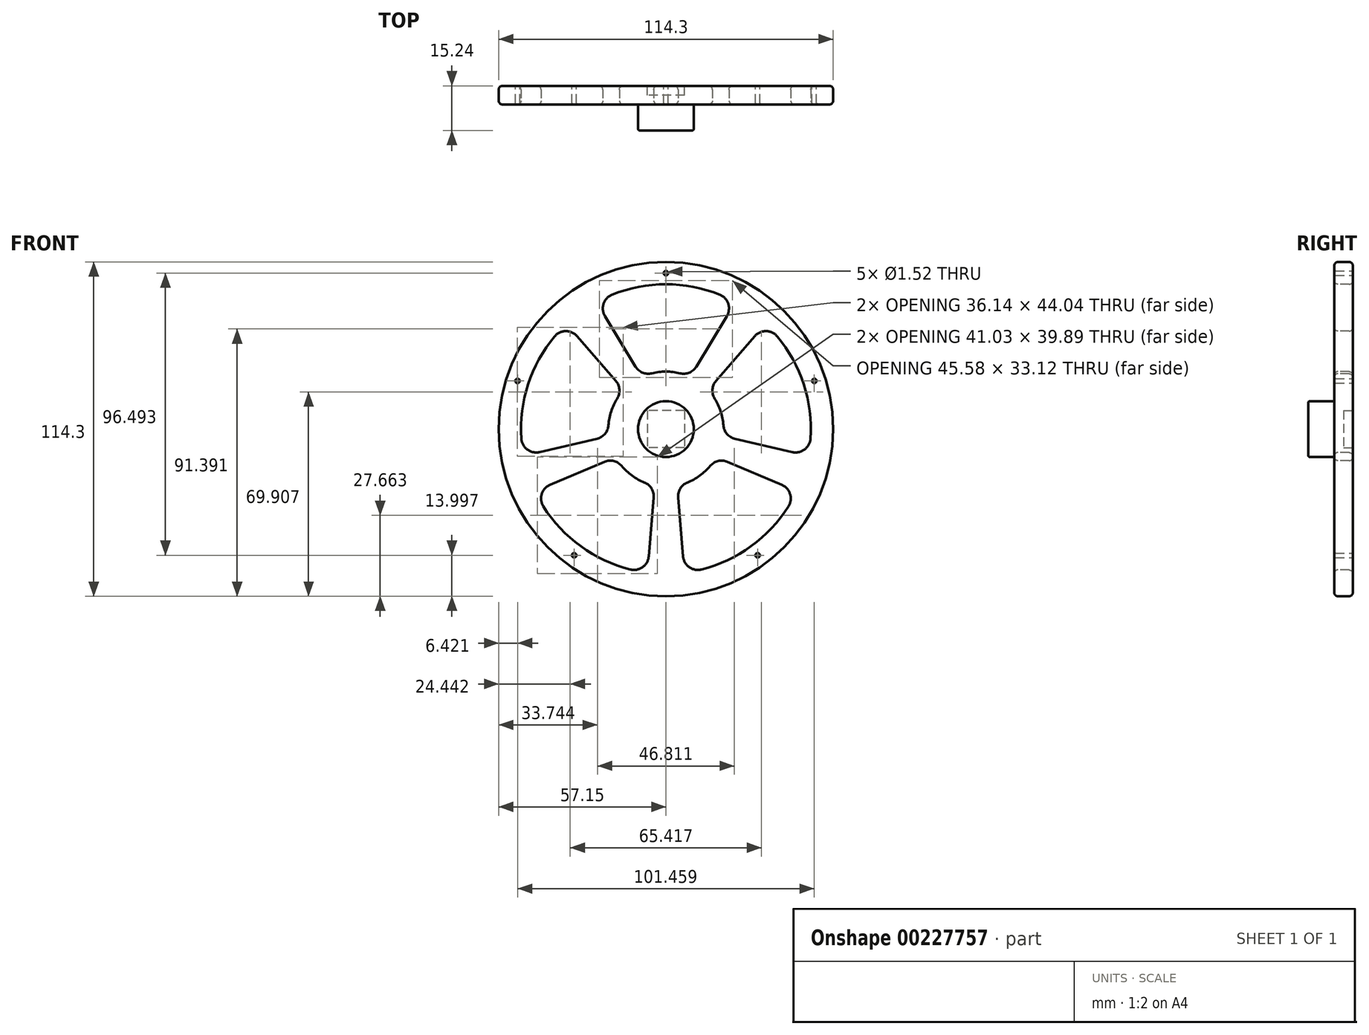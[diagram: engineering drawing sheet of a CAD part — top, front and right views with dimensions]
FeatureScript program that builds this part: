
annotation { "Feature Type Name" : "Feature", "Feature Type Description" : "" }
export const myFeature = defineFeature(function(context is Context, id is Id, definition is map)
    precondition{}
    {
        {
            var Q0;
            Q0=qCreatedBy(makeId("Front.planeOp"),FACE);
            var sketch = newSketch(context, id + "F0", { "sketchPlane" : qUnion([Q0])});
            skCircle(sketch, "E0", {"center": v(0, 0) * mm, "radius": 57.15 * mm});
            skSolve(sketch);
        }
        {
            var Q0;
            Q0=qSketchRegion(id+"F0",true);
            extrude(context, id + "F1", {"entities" : qUnion([Q0]), "depth" : 6.35 * mm});
        }
        {
            var Q0;
            Q0=makeQuery(id+"F1.opExtrude","CAP_FACE",FACE,{"disambiguationData":[OSD([sQuery(id+"F0.wireOp",EDGE,"E0")])],"isStart":false});
            var sketch = newSketch(context, id + "F2", { "sketchPlane" : qUnion([Q0])});
            skCircle(sketch, "E1", {"center": v(0, 0) * mm, "radius": 9.53 * mm});
            skSolve(sketch);
        }
        {
            var Q0;
            Q0=qSketchRegion(id+"F2",true);
            extrude(context, id + "F3", {"entities" : qUnion([Q0]), "operationType" : NewBodyOperationType.ADD, "depth" : 8.9 * mm});
        }
        {
            var Q0;
            Q0=makeQuery(id+"F1.opExtrude","CAP_FACE",FACE,{"disambiguationData":[OSD([sQuery(id+"F0.wireOp",EDGE,"E0")])],"isStart":true});
            var sketch = newSketch(context, id + "F4", { "sketchPlane" : qUnion([Q0])});
            skCircle(sketch, "E2", {"center": v(0, 53.34) * mm, "radius": 0.76 * mm});
            skCircle(sketch, "E3.1.0", {"center": v(-50.73, 16.48) * mm, "radius": 0.76 * mm});
            skCircle(sketch, "E3.2.0", {"center": v(-31.35, -43.15) * mm, "radius": 0.76 * mm});
            skCircle(sketch, "E3.3.0", {"center": v(31.35, -43.15) * mm, "radius": 0.76 * mm});
            skCircle(sketch, "E3.4.0", {"center": v(50.73, 16.48) * mm, "radius": 0.76 * mm});
            skPoint(sketch, "E3.center", {"position": v(0, 0) * mm});
            skSolve(sketch);
        }
        {
            var Q0;
            Q0=qSketchRegion(id+"F4",true);
            extrude(context, id + "F5", {"entities" : qUnion([Q0]), "operationType" : NewBodyOperationType.REMOVE, "endBound" : BoundingType.THROUGH_ALL, "oppositeDirection" : true, "depth" : 25.4 * mm});
        }
        {
            var Q0;
            Q0=makeQuery(id+"F1.opExtrude","CAP_FACE",FACE,{"disambiguationData":[OSD([sQuery(id+"F0.wireOp",EDGE,"E0")])],"isStart":false});
            var sketch = newSketch(context, id + "F6", { "sketchPlane" : qUnion([Q0])});
            skArc(sketch, "E4", {"start": v(-14.43, 13.38) * mm, "mid": v(-18.72, 6.08) * mm, "end": v(-19.54, -2.34) * mm});
            skArc(sketch, "E5", {"start": v(-34.01, 36) * mm, "mid": v(-47.1, 15.3) * mm, "end": v(-48.68, -9.14) * mm});
            skLineSegment(sketch, "E6", {"start": v(-3.8, -19.31) * mm, "end": v(-6.35, -49.12) * mm});
            skLineSegment(sketch, "E7", {"start": v(3.8, -19.31) * mm, "end": v(6.35, -49.12) * mm});
            skLineSegment(sketch, "E8.1.0", {"start": v(17.2, -9.6) * mm, "end": v(44.75, -21.22) * mm});
            skLineSegment(sketch, "E8.1.1", {"start": v(19.54, -2.34) * mm, "end": v(48.68, -9.14) * mm});
            skLineSegment(sketch, "E8.2.0", {"start": v(14.43, 13.38) * mm, "end": v(34.01, 36) * mm});
            skLineSegment(sketch, "E8.2.1", {"start": v(8.27, 17.86) * mm, "end": v(23.74, 43.47) * mm});
            skLineSegment(sketch, "E8.3.0", {"start": v(-8.27, 17.86) * mm, "end": v(-23.74, 43.47) * mm});
            skLineSegment(sketch, "E8.3.1", {"start": v(-14.43, 13.38) * mm, "end": v(-34.01, 36) * mm});
            skLineSegment(sketch, "E8.4.0", {"start": v(-19.54, -2.34) * mm, "end": v(-48.68, -9.14) * mm});
            skLineSegment(sketch, "E8.4.1", {"start": v(-17.2, -9.6) * mm, "end": v(-44.75, -21.22) * mm});
            skArc(sketch, "E9.trimOffspring", {"start": v(8.27, 17.86) * mm, "mid": v(0, 19.69) * mm, "end": v(-8.27, 17.86) * mm});
            skArc(sketch, "E10.trimOffspring", {"start": v(23.74, 43.47) * mm, "mid": v(0, 49.53) * mm, "end": v(-23.74, 43.47) * mm});
            skArc(sketch, "E11.trimOffspring", {"start": v(48.68, -9.14) * mm, "mid": v(47.1, 15.3) * mm, "end": v(34.01, 36) * mm});
            skArc(sketch, "E12.trimOffspring", {"start": v(19.54, -2.34) * mm, "mid": v(18.72, 6.08) * mm, "end": v(14.43, 13.38) * mm});
            skArc(sketch, "E13.trimOffspring", {"start": v(3.81, -19.31) * mm, "mid": v(11.57, -15.93) * mm, "end": v(17.2, -9.6) * mm});
            skArc(sketch, "E14.trimOffspring", {"start": v(6.35, -49.12) * mm, "mid": v(29.11, -40.07) * mm, "end": v(44.75, -21.22) * mm});
            skArc(sketch, "E15.trimOffspring", {"start": v(-44.75, -21.22) * mm, "mid": v(-29.11, -40.07) * mm, "end": v(-6.35, -49.12) * mm});
            skArc(sketch, "E16.trimOffspring", {"start": v(-17.2, -9.6) * mm, "mid": v(-11.57, -15.93) * mm, "end": v(-3.81, -19.31) * mm});
            skSolve(sketch);
        }
        {
            var Q0;
            Q0=qSketchRegion(id+"F6",true);
            extrude(context, id + "F7", {"entities" : qUnion([Q0]), "operationType" : NewBodyOperationType.REMOVE, "oppositeDirection" : true, "depth" : 25.4 * mm});
        }
        {
            var Q0;
            Q0=makeQuery(id+"F7.boolean.opBoolean","COPY",EDGE,{"derivedFrom":makeQuery(id+"F7.opExtrude","SWEPT_EDGE",EDGE,{"disambiguationData":[OSD([sQuery(id+"F6.wireOp",EDGE,"E8.3.0"),sQuery(id+"F6.wireOp",EDGE,"E9.trimOffspring")])]})});
            var Q1;
            Q1=makeQuery(id+"F7.boolean.opBoolean","COPY",EDGE,{"derivedFrom":makeQuery(id+"F7.opExtrude","SWEPT_EDGE",EDGE,{"disambiguationData":[OSD([sQuery(id+"F6.wireOp",EDGE,"E8.2.1"),sQuery(id+"F6.wireOp",EDGE,"E9.trimOffspring")])]})});
            var Q2;
            Q2=makeQuery(id+"F7.boolean.opBoolean","COPY",EDGE,{"derivedFrom":makeQuery(id+"F7.opExtrude","SWEPT_EDGE",EDGE,{"disambiguationData":[OSD([sQuery(id+"F6.wireOp",EDGE,"E8.3.0"),sQuery(id+"F6.wireOp",EDGE,"E10.trimOffspring")])]})});
            var Q3;
            Q3=makeQuery(id+"F7.boolean.opBoolean","COPY",EDGE,{"derivedFrom":makeQuery(id+"F7.opExtrude","SWEPT_EDGE",EDGE,{"disambiguationData":[OSD([sQuery(id+"F6.wireOp",EDGE,"E8.2.1"),sQuery(id+"F6.wireOp",EDGE,"E10.trimOffspring")])]})});
            var Q4;
            Q4=makeQuery(id+"F7.boolean.opBoolean","COPY",EDGE,{"derivedFrom":makeQuery(id+"F7.opExtrude","SWEPT_EDGE",EDGE,{"disambiguationData":[OSD([sQuery(id+"F6.wireOp",EDGE,"E8.2.0"),sQuery(id+"F6.wireOp",EDGE,"E11.trimOffspring")])]})});
            var Q5;
            Q5=makeQuery(id+"F7.boolean.opBoolean","COPY",EDGE,{"derivedFrom":makeQuery(id+"F7.opExtrude","SWEPT_EDGE",EDGE,{"disambiguationData":[OSD([sQuery(id+"F6.wireOp",EDGE,"E8.2.0"),sQuery(id+"F6.wireOp",EDGE,"E12.trimOffspring")])]})});
            var Q6;
            Q6=makeQuery(id+"F7.boolean.opBoolean","COPY",EDGE,{"derivedFrom":makeQuery(id+"F7.opExtrude","SWEPT_EDGE",EDGE,{"disambiguationData":[OSD([sQuery(id+"F6.wireOp",EDGE,"E8.1.1"),sQuery(id+"F6.wireOp",EDGE,"E12.trimOffspring")])]})});
            var Q7;
            Q7=makeQuery(id+"F7.boolean.opBoolean","COPY",EDGE,{"derivedFrom":makeQuery(id+"F7.opExtrude","SWEPT_EDGE",EDGE,{"disambiguationData":[OSD([sQuery(id+"F6.wireOp",EDGE,"E8.1.1"),sQuery(id+"F6.wireOp",EDGE,"E11.trimOffspring")])]})});
            var Q8;
            Q8=makeQuery(id+"F7.boolean.opBoolean","COPY",EDGE,{"derivedFrom":makeQuery(id+"F7.opExtrude","SWEPT_EDGE",EDGE,{"disambiguationData":[OSD([sQuery(id+"F6.wireOp",EDGE,"E8.1.0"),sQuery(id+"F6.wireOp",EDGE,"E14.trimOffspring")])]})});
            var Q9;
            Q9=makeQuery(id+"F7.boolean.opBoolean","COPY",EDGE,{"derivedFrom":makeQuery(id+"F7.opExtrude","SWEPT_EDGE",EDGE,{"disambiguationData":[OSD([sQuery(id+"F6.wireOp",EDGE,"E7"),sQuery(id+"F6.wireOp",EDGE,"E14.trimOffspring")])]})});
            var Q10;
            Q10=makeQuery(id+"F7.boolean.opBoolean","COPY",EDGE,{"derivedFrom":makeQuery(id+"F7.opExtrude","SWEPT_EDGE",EDGE,{"disambiguationData":[OSD([sQuery(id+"F6.wireOp",EDGE,"E7"),sQuery(id+"F6.wireOp",EDGE,"E13.trimOffspring")])]})});
            var Q11;
            Q11=makeQuery(id+"F7.boolean.opBoolean","COPY",EDGE,{"derivedFrom":makeQuery(id+"F7.opExtrude","SWEPT_EDGE",EDGE,{"disambiguationData":[OSD([sQuery(id+"F6.wireOp",EDGE,"E8.1.0"),sQuery(id+"F6.wireOp",EDGE,"E13.trimOffspring")])]})});
            var Q12;
            Q12=makeQuery(id+"F7.boolean.opBoolean","COPY",EDGE,{"derivedFrom":makeQuery(id+"F7.opExtrude","SWEPT_EDGE",EDGE,{"disambiguationData":[OSD([sQuery(id+"F6.wireOp",EDGE,"E8.4.1"),sQuery(id+"F6.wireOp",EDGE,"E16.trimOffspring")])]})});
            var Q13;
            Q13=makeQuery(id+"F7.boolean.opBoolean","COPY",EDGE,{"derivedFrom":makeQuery(id+"F7.opExtrude","SWEPT_EDGE",EDGE,{"disambiguationData":[OSD([sQuery(id+"F6.wireOp",EDGE,"E6"),sQuery(id+"F6.wireOp",EDGE,"E16.trimOffspring")])]})});
            var Q14;
            Q14=makeQuery(id+"F7.boolean.opBoolean","COPY",EDGE,{"derivedFrom":makeQuery(id+"F7.opExtrude","SWEPT_EDGE",EDGE,{"disambiguationData":[OSD([sQuery(id+"F6.wireOp",EDGE,"E6"),sQuery(id+"F6.wireOp",EDGE,"E15.trimOffspring")])]})});
            var Q15;
            Q15=makeQuery(id+"F7.boolean.opBoolean","COPY",EDGE,{"derivedFrom":makeQuery(id+"F7.opExtrude","SWEPT_EDGE",EDGE,{"disambiguationData":[OSD([sQuery(id+"F6.wireOp",EDGE,"E8.4.1"),sQuery(id+"F6.wireOp",EDGE,"E15.trimOffspring")])]})});
            var Q16;
            Q16=makeQuery(id+"F7.boolean.opBoolean","COPY",EDGE,{"derivedFrom":makeQuery(id+"F7.opExtrude","SWEPT_EDGE",EDGE,{"disambiguationData":[OSD([sQuery(id+"F6.wireOp",EDGE,"E5"),sQuery(id+"F6.wireOp",EDGE,"E8.4.0")])]})});
            var Q17;
            Q17=makeQuery(id+"F7.boolean.opBoolean","COPY",EDGE,{"derivedFrom":makeQuery(id+"F7.opExtrude","SWEPT_EDGE",EDGE,{"disambiguationData":[OSD([sQuery(id+"F6.wireOp",EDGE,"E4"),sQuery(id+"F6.wireOp",EDGE,"E8.4.0")])]})});
            var Q18;
            Q18=makeQuery(id+"F7.boolean.opBoolean","COPY",EDGE,{"derivedFrom":makeQuery(id+"F7.opExtrude","SWEPT_EDGE",EDGE,{"disambiguationData":[OSD([sQuery(id+"F6.wireOp",EDGE,"E4"),sQuery(id+"F6.wireOp",EDGE,"E8.3.1")])]})});
            var Q19;
            Q19=makeQuery(id+"F7.boolean.opBoolean","COPY",EDGE,{"derivedFrom":makeQuery(id+"F7.opExtrude","SWEPT_EDGE",EDGE,{"disambiguationData":[OSD([sQuery(id+"F6.wireOp",EDGE,"E5"),sQuery(id+"F6.wireOp",EDGE,"E8.3.1")])]})});
            fillet(context, id + "F8", {"entities" : qUnion([Q0, Q1, Q2, Q3, Q4, Q5, Q6, Q7, Q8, Q9, Q10, Q11, Q12, Q13, Q14, Q15, Q16, Q17, Q18, Q19]), "radius" : 5.08 * mm, "tangentPropagation" : true, "allowEdgeOverflow" : false});
        }
        {
            var Q0;
            Q0=makeQuery(id+"F1.opExtrude","CAP_EDGE",EDGE,{"disambiguationData":[OSD([sQuery(id+"F0.wireOp",EDGE,"E0")])],"isStart":false});
            var Q1;
            Q1=makeQuery(id+"F8.opFillet","BLEND_EDGE",EDGE,{"blendedFrom":[makeQuery(id+"F7.boolean.opBoolean","COPY",EDGE,{"derivedFrom":makeQuery(id+"F7.opExtrude","SWEPT_EDGE",EDGE,{"disambiguationData":[OSD([sQuery(id+"F6.wireOp",EDGE,"E8.2.0"),sQuery(id+"F6.wireOp",EDGE,"E11.trimOffspring")])]})}),makeQuery(id+"F1.opExtrude","CAP_FACE",FACE,{"disambiguationData":[OSD([sQuery(id+"F0.wireOp",EDGE,"E0")])],"isStart":false})],"blendedInto":[makeQuery(id+"F1.opExtrude","CAP_FACE",FACE,{"disambiguationData":[OSD([sQuery(id+"F0.wireOp",EDGE,"E0")])],"isStart":false})]});
            var Q2;
            Q2=makeQuery(id+"F8.opFillet","BLEND_EDGE",EDGE,{"blendedFrom":[makeQuery(id+"F7.boolean.opBoolean","COPY",EDGE,{"derivedFrom":makeQuery(id+"F7.opExtrude","SWEPT_EDGE",EDGE,{"disambiguationData":[OSD([sQuery(id+"F6.wireOp",EDGE,"E8.2.1"),sQuery(id+"F6.wireOp",EDGE,"E9.trimOffspring")])]})}),makeQuery(id+"F1.opExtrude","CAP_FACE",FACE,{"disambiguationData":[OSD([sQuery(id+"F0.wireOp",EDGE,"E0")])],"isStart":false})],"blendedInto":[makeQuery(id+"F1.opExtrude","CAP_FACE",FACE,{"disambiguationData":[OSD([sQuery(id+"F0.wireOp",EDGE,"E0")])],"isStart":false})]});
            var Q3;
            Q3=makeQuery(id+"F8.opFillet","BLEND_EDGE",EDGE,{"blendedFrom":[makeQuery(id+"F7.boolean.opBoolean","COPY",EDGE,{"derivedFrom":makeQuery(id+"F7.opExtrude","SWEPT_EDGE",EDGE,{"disambiguationData":[OSD([sQuery(id+"F6.wireOp",EDGE,"E8.1.0"),sQuery(id+"F6.wireOp",EDGE,"E13.trimOffspring")])]})}),makeQuery(id+"F1.opExtrude","CAP_FACE",FACE,{"disambiguationData":[OSD([sQuery(id+"F0.wireOp",EDGE,"E0")])],"isStart":false})],"blendedInto":[makeQuery(id+"F1.opExtrude","CAP_FACE",FACE,{"disambiguationData":[OSD([sQuery(id+"F0.wireOp",EDGE,"E0")])],"isStart":false})]});
            var Q4;
            Q4=makeQuery(id+"F8.opFillet","BLEND_EDGE",EDGE,{"blendedFrom":[makeQuery(id+"F7.boolean.opBoolean","COPY",EDGE,{"derivedFrom":makeQuery(id+"F7.opExtrude","SWEPT_EDGE",EDGE,{"disambiguationData":[OSD([sQuery(id+"F6.wireOp",EDGE,"E8.4.1"),sQuery(id+"F6.wireOp",EDGE,"E16.trimOffspring")])]})}),makeQuery(id+"F1.opExtrude","CAP_FACE",FACE,{"disambiguationData":[OSD([sQuery(id+"F0.wireOp",EDGE,"E0")])],"isStart":false})],"blendedInto":[makeQuery(id+"F1.opExtrude","CAP_FACE",FACE,{"disambiguationData":[OSD([sQuery(id+"F0.wireOp",EDGE,"E0")])],"isStart":false})]});
            var Q5;
            Q5=makeQuery(id+"F8.opFillet","BLEND_EDGE",EDGE,{"blendedFrom":[makeQuery(id+"F7.boolean.opBoolean","COPY",EDGE,{"derivedFrom":makeQuery(id+"F7.opExtrude","SWEPT_EDGE",EDGE,{"disambiguationData":[OSD([sQuery(id+"F6.wireOp",EDGE,"E4"),sQuery(id+"F6.wireOp",EDGE,"E8.3.1")])]})}),makeQuery(id+"F1.opExtrude","CAP_FACE",FACE,{"disambiguationData":[OSD([sQuery(id+"F0.wireOp",EDGE,"E0")])],"isStart":false})],"blendedInto":[makeQuery(id+"F1.opExtrude","CAP_FACE",FACE,{"disambiguationData":[OSD([sQuery(id+"F0.wireOp",EDGE,"E0")])],"isStart":false})]});
            var Q6;
            Q6=makeQuery(id+"F7.boolean.opBoolean","INTERSECT",EDGE,{"derivedFrom":[makeQuery(id+"F1.opExtrude","CAP_FACE",FACE,{"disambiguationData":[OSD([sQuery(id+"F0.wireOp",EDGE,"E0")])],"isStart":true}),makeQuery(id+"F7.opExtrude","SWEPT_FACE",FACE,{"disambiguationData":[OSD([sQuery(id+"F6.wireOp",EDGE,"E10.trimOffspring")])]})]});
            var Q7;
            Q7=makeQuery(id+"F7.boolean.opBoolean","INTERSECT",EDGE,{"derivedFrom":[makeQuery(id+"F1.opExtrude","CAP_FACE",FACE,{"disambiguationData":[OSD([sQuery(id+"F0.wireOp",EDGE,"E0")])],"isStart":true}),makeQuery(id+"F7.opExtrude","SWEPT_FACE",FACE,{"disambiguationData":[OSD([sQuery(id+"F6.wireOp",EDGE,"E8.2.0")])]})]});
            var Q8;
            Q8=makeQuery(id+"F7.boolean.opBoolean","INTERSECT",EDGE,{"derivedFrom":[makeQuery(id+"F1.opExtrude","CAP_FACE",FACE,{"disambiguationData":[OSD([sQuery(id+"F0.wireOp",EDGE,"E0")])],"isStart":true}),makeQuery(id+"F7.opExtrude","SWEPT_FACE",FACE,{"disambiguationData":[OSD([sQuery(id+"F6.wireOp",EDGE,"E8.1.0")])]})]});
            var Q9;
            Q9=makeQuery(id+"F8.opFillet","BLEND_EDGE",EDGE,{"blendedFrom":[makeQuery(id+"F7.boolean.opBoolean","COPY",EDGE,{"derivedFrom":makeQuery(id+"F7.opExtrude","SWEPT_EDGE",EDGE,{"disambiguationData":[OSD([sQuery(id+"F6.wireOp",EDGE,"E6"),sQuery(id+"F6.wireOp",EDGE,"E16.trimOffspring")])]})}),makeQuery(id+"F1.opExtrude","CAP_FACE",FACE,{"disambiguationData":[OSD([sQuery(id+"F0.wireOp",EDGE,"E0")])],"isStart":true})],"blendedInto":[makeQuery(id+"F1.opExtrude","CAP_FACE",FACE,{"disambiguationData":[OSD([sQuery(id+"F0.wireOp",EDGE,"E0")])],"isStart":true})]});
            var Q10;
            Q10=makeQuery(id+"F7.boolean.opBoolean","INTERSECT",EDGE,{"derivedFrom":[makeQuery(id+"F1.opExtrude","CAP_FACE",FACE,{"disambiguationData":[OSD([sQuery(id+"F0.wireOp",EDGE,"E0")])],"isStart":true}),makeQuery(id+"F7.opExtrude","SWEPT_FACE",FACE,{"disambiguationData":[OSD([sQuery(id+"F6.wireOp",EDGE,"E8.3.1")])]})]});
            var Q11;
            Q11=makeQuery(id+"F1.opExtrude","CAP_EDGE",EDGE,{"disambiguationData":[OSD([sQuery(id+"F0.wireOp",EDGE,"E0")])],"isStart":true});
            fillet(context, id + "F9", {"entities" : qUnion([Q0, Q1, Q2, Q3, Q4, Q5, Q6, Q7, Q8, Q9, Q10, Q11]), "radius" : 1.27 * mm, "tangentPropagation" : true, "allowEdgeOverflow" : false});
        }
        {
            var Q0;
            Q0=makeQuery(id+"F5.boolean.opBoolean","COPY",EDGE,{"derivedFrom":makeQuery(id+"F5.opExtrude","CAP_EDGE",EDGE,{"disambiguationData":[OSD([sQuery(id+"F4.wireOp",EDGE,"E3.1.0")])],"isStart":true})});
            var Q1;
            Q1=makeQuery(id+"F5.boolean.opBoolean","COPY",EDGE,{"derivedFrom":makeQuery(id+"F5.opExtrude","CAP_EDGE",EDGE,{"disambiguationData":[OSD([sQuery(id+"F4.wireOp",EDGE,"E2")])],"isStart":true})});
            var Q2;
            Q2=makeQuery(id+"F5.boolean.opBoolean","COPY",EDGE,{"derivedFrom":makeQuery(id+"F5.opExtrude","CAP_EDGE",EDGE,{"disambiguationData":[OSD([sQuery(id+"F4.wireOp",EDGE,"E3.4.0")])],"isStart":true})});
            var Q3;
            Q3=makeQuery(id+"F5.boolean.opBoolean","COPY",EDGE,{"derivedFrom":makeQuery(id+"F5.opExtrude","CAP_EDGE",EDGE,{"disambiguationData":[OSD([sQuery(id+"F4.wireOp",EDGE,"E3.3.0")])],"isStart":true})});
            var Q4;
            Q4=makeQuery(id+"F5.boolean.opBoolean","COPY",EDGE,{"derivedFrom":makeQuery(id+"F5.opExtrude","CAP_EDGE",EDGE,{"disambiguationData":[OSD([sQuery(id+"F4.wireOp",EDGE,"E3.2.0")])],"isStart":true})});
            var Q5;
            Q5=makeQuery(id+"F5.boolean.opBoolean","INTERSECT",EDGE,{"derivedFrom":[makeQuery(id+"F1.opExtrude","CAP_FACE",FACE,{"disambiguationData":[OSD([sQuery(id+"F0.wireOp",EDGE,"E0")])],"isStart":false}),makeQuery(id+"F5.opExtrude","SWEPT_FACE",FACE,{"disambiguationData":[OSD([sQuery(id+"F4.wireOp",EDGE,"E3.3.0")])]})]});
            var Q6;
            Q6=makeQuery(id+"F5.boolean.opBoolean","INTERSECT",EDGE,{"derivedFrom":[makeQuery(id+"F1.opExtrude","CAP_FACE",FACE,{"disambiguationData":[OSD([sQuery(id+"F0.wireOp",EDGE,"E0")])],"isStart":false}),makeQuery(id+"F5.opExtrude","SWEPT_FACE",FACE,{"disambiguationData":[OSD([sQuery(id+"F4.wireOp",EDGE,"E3.2.0")])]})]});
            var Q7;
            Q7=makeQuery(id+"F5.boolean.opBoolean","INTERSECT",EDGE,{"derivedFrom":[makeQuery(id+"F1.opExtrude","CAP_FACE",FACE,{"disambiguationData":[OSD([sQuery(id+"F0.wireOp",EDGE,"E0")])],"isStart":false}),makeQuery(id+"F5.opExtrude","SWEPT_FACE",FACE,{"disambiguationData":[OSD([sQuery(id+"F4.wireOp",EDGE,"E3.1.0")])]})]});
            var Q8;
            Q8=makeQuery(id+"F5.boolean.opBoolean","INTERSECT",EDGE,{"derivedFrom":[makeQuery(id+"F1.opExtrude","CAP_FACE",FACE,{"disambiguationData":[OSD([sQuery(id+"F0.wireOp",EDGE,"E0")])],"isStart":false}),makeQuery(id+"F5.opExtrude","SWEPT_FACE",FACE,{"disambiguationData":[OSD([sQuery(id+"F4.wireOp",EDGE,"E2")])]})]});
            var Q9;
            Q9=makeQuery(id+"F5.boolean.opBoolean","INTERSECT",EDGE,{"derivedFrom":[makeQuery(id+"F1.opExtrude","CAP_FACE",FACE,{"disambiguationData":[OSD([sQuery(id+"F0.wireOp",EDGE,"E0")])],"isStart":false}),makeQuery(id+"F5.opExtrude","SWEPT_FACE",FACE,{"disambiguationData":[OSD([sQuery(id+"F4.wireOp",EDGE,"E3.4.0")])]})]});
            var Q10;
            Q10=makeQuery(id+"F3.opExtrude","CAP_EDGE",EDGE,{"disambiguationData":[OSD([sQuery(id+"F2.wireOp",EDGE,"E1")])],"isStart":true});
            var Q11;
            Q11=makeQuery(id+"F3.opExtrude","CAP_EDGE",EDGE,{"disambiguationData":[OSD([sQuery(id+"F2.wireOp",EDGE,"E1")])],"isStart":false});
            var Q12;
            Q12=makeQuery(id+"FeMQh0gbYnoDPlp_1.boolean.opBoolean","COPY",EDGE,{"derivedFrom":makeQuery(id+"FeMQh0gbYnoDPlp_1.opExtrude","CAP_EDGE",EDGE,{"disambiguationData":[OSD([sQuery(id+"F2RVRRPv2SC6N3P_1.wireOp",EDGE,"fKLkzBig-sDHv-PITV-xeHw-v5L786XIfZfO")])],"isStart":true})});
            var Q13;
            Q13=makeQuery(id+"FZ4jULmNcCfVgcP_1.boolean.opBoolean","INTERSECT",EDGE,{"disambiguationData":[OD(0.0)],"derivedFrom":[makeQuery(id+"FeMQh0gbYnoDPlp_1.boolean.opBoolean","COPY",FACE,{"derivedFrom":makeQuery(id+"FeMQh0gbYnoDPlp_1.opExtrude","SWEPT_FACE",FACE,{"disambiguationData":[OSD([sQuery(id+"F2RVRRPv2SC6N3P_1.wireOp",EDGE,"fKLkzBig-sDHv-PITV-xeHw-v5L786XIfZfO")])]})}),makeQuery(id+"FZ4jULmNcCfVgcP_1.opExtrude","SWEPT_FACE",FACE,{"disambiguationData":[OSD([sQuery(id+"Fmu1I0555Jz0ejQ_1.wireOp",EDGE,"1qAzPiUb-8Gs9-xsMG-hmAk-HbD23xbOJPvn")])]})]});
            var Q14;
            Q14=makeQuery(id+"FZ4jULmNcCfVgcP_1.boolean.opBoolean","INTERSECT",EDGE,{"disambiguationData":[OD(1.0)],"derivedFrom":[makeQuery(id+"FeMQh0gbYnoDPlp_1.boolean.opBoolean","COPY",FACE,{"derivedFrom":makeQuery(id+"FeMQh0gbYnoDPlp_1.opExtrude","SWEPT_FACE",FACE,{"disambiguationData":[OSD([sQuery(id+"F2RVRRPv2SC6N3P_1.wireOp",EDGE,"fKLkzBig-sDHv-PITV-xeHw-v5L786XIfZfO")])]})}),makeQuery(id+"FZ4jULmNcCfVgcP_1.opExtrude","SWEPT_FACE",FACE,{"disambiguationData":[OSD([sQuery(id+"Fmu1I0555Jz0ejQ_1.wireOp",EDGE,"1qAzPiUb-8Gs9-xsMG-hmAk-HbD23xbOJPvn")])]})]});
            var Q15;
            Q15=makeQuery(id+"FZ4jULmNcCfVgcP_1.boolean.opBoolean","INTERSECT",EDGE,{"disambiguationData":[OD(1.0)],"derivedFrom":[makeQuery(id+"F3.opExtrude","SWEPT_FACE",FACE,{"disambiguationData":[OSD([sQuery(id+"F2.wireOp",EDGE,"E1")])]}),makeQuery(id+"FZ4jULmNcCfVgcP_1.opExtrude","SWEPT_FACE",FACE,{"disambiguationData":[OSD([sQuery(id+"Fmu1I0555Jz0ejQ_1.wireOp",EDGE,"1qAzPiUb-8Gs9-xsMG-hmAk-HbD23xbOJPvn")])]})]});
            fillet(context, id + "F10", {"entities" : qUnion([Q0, Q1, Q2, Q3, Q4, Q5, Q6, Q7, Q8, Q9, Q10, Q11, Q12, Q13, Q14, Q15]), "radius" : 0.5 * mm, "tangentPropagation" : true, "allowEdgeOverflow" : false});
        }
        {
            var Q0;
            Q0=makeQuery(id+"F1.opExtrude","CAP_FACE",FACE,{"disambiguationData":[OSD([sQuery(id+"F0.wireOp",EDGE,"E0")])],"isStart":true});
            var sketch = newSketch(context, id + "F11", { "sketchPlane" : qUnion([Q0])});
            skLineSegment(sketch, "E17.bottom", {"start": v(-6.35, 6.35) * mm, "end": v(6.35, 6.35) * mm});
            skLineSegment(sketch, "E17.top", {"start": v(-6.35, -6.35) * mm, "end": v(6.35, -6.35) * mm});
            skLineSegment(sketch, "E17.left", {"start": v(-6.35, 6.35) * mm, "end": v(-6.35, -6.35) * mm});
            skLineSegment(sketch, "E17.right", {"start": v(6.35, 6.35) * mm, "end": v(6.35, -6.35) * mm});
            skSolve(sketch);
        }
        {
            var Q0;
            Q0=qSketchRegion(id+"F11",true);
            extrude(context, id + "F12", {"entities" : qUnion([Q0]), "operationType" : NewBodyOperationType.REMOVE, "oppositeDirection" : true, "depth" : 3.17 * mm});
        }
    });
